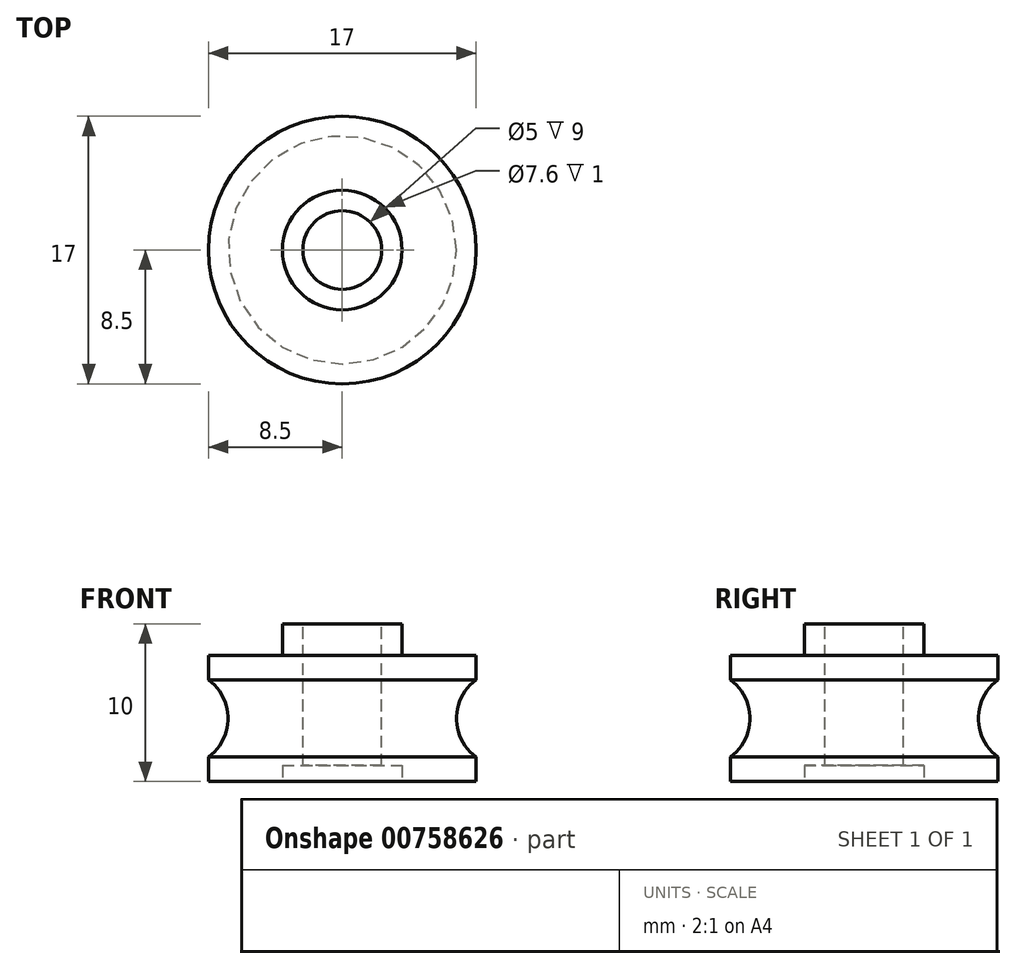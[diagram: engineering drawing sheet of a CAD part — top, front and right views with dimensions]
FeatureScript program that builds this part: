
annotation { "Feature Type Name" : "Feature", "Feature Type Description" : "" }
export const myFeature = defineFeature(function(context is Context, id is Id, definition is map)
    precondition{}
    {
        {
            var Q0;
            Q0=qCreatedBy(makeId("Top.planeOp"),FACE);
            var sketch = newSketch(context, id + "F0", { "sketchPlane" : qUnion([Q0])});
            skCircle(sketch, "E0", {"center": v(0, 0) * mm, "radius": 8.5 * mm});
            skSolve(sketch);
        }
        {
            var Q0;
            Q0=makeQuery(id+"F0.imprint","IMPRINT",FACE,{"disambiguationData":[TD([[makeQuery(id+"F0.imprint","IMPRINT",EDGE,{"derivedFrom":sQuery(id+"F0.wireOp",EDGE,"E0")}),1.0]])]});
            extrude(context, id + "F1", {"entities" : qUnion([Q0]), "depth" : 8 * mm, "offsetDistance" : 25 * mm});
        }
        {
            var Q0;
            Q0=makeQuery(id+"F1.opExtrude","CAP_FACE",FACE,{"disambiguationData":[OSD([sQuery(id+"F0.wireOp",EDGE,"E0")])],"isStart":false});
            var sketch = newSketch(context, id + "F2", { "sketchPlane" : qUnion([Q0])});
            skCircle(sketch, "E1", {"center": v(0, 0) * mm, "radius": 3.8 * mm});
            skSolve(sketch);
        }
        {
            var Q0;
            Q0=makeQuery(id+"F2.imprint","IMPRINT",FACE,{"disambiguationData":[TD([[makeQuery(id+"F2.imprint","IMPRINT",EDGE,{"derivedFrom":sQuery(id+"F2.wireOp",EDGE,"E1")}),1.0]])]});
            extrude(context, id + "F3", {"entities" : qUnion([Q0]), "operationType" : NewBodyOperationType.ADD, "depth" : 2 * mm, "offsetDistance" : 25 * mm});
        }
        {
            var Q0;
            Q0=makeQuery(id+"F3.opExtrude","CAP_FACE",FACE,{"disambiguationData":[OSD([sQuery(id+"F2.wireOp",EDGE,"E1")])],"isStart":false});
            var sketch = newSketch(context, id + "F4", { "sketchPlane" : qUnion([Q0])});
            skCircle(sketch, "E2", {"center": v(0, 0) * mm, "radius": 2.5 * mm});
            skSolve(sketch);
        }
        {
            var Q0;
            Q0=makeQuery(id+"F4.imprint","IMPRINT",FACE,{"disambiguationData":[TD([[makeQuery(id+"F4.imprint","IMPRINT",EDGE,{"derivedFrom":sQuery(id+"F4.wireOp",EDGE,"E2")}),1.0]])]});
            extrude(context, id + "F5", {"entities" : qUnion([Q0]), "operationType" : NewBodyOperationType.REMOVE, "endBound" : BoundingType.THROUGH_ALL, "oppositeDirection" : true, "depth" : 25 * mm, "offsetDistance" : 25 * mm});
        }
        {
            var Q0;
            Q0=qCreatedBy(makeId("Right.planeOp"),FACE);
            var sketch = newSketch(context, id + "F6", { "sketchPlane" : qUnion([Q0])});
            skCircle(sketch, "E3", {"center": v(-10.25, 4) * mm, "radius": 3 * mm});
            skPoint(sketch, "E4.middle", {"position": v(0, 0) * mm});
            skLineSegment(sketch, "E5", {"start": v(0, 0) * mm, "end": v(0, 15.8) * mm});
            skSolve(sketch);
        }
        {
            var Q0;
            Q0=makeQuery(id+"F6.imprint","IMPRINT",FACE,{"disambiguationData":[TD([[makeQuery(id+"F6.imprint","IMPRINT",EDGE,{"derivedFrom":sQuery(id+"F6.wireOp",EDGE,"E3")}),1.0]])]});
            var Q1;
            Q1=sQuery(id+"F6.wireOp",EDGE,"E5");
            revolve(context, id + "F7", {"operationType" : NewBodyOperationType.REMOVE, "surfaceOperationType" : NewSurfaceOperationType.NEW, "entities" : qUnion([Q0]), "axis" : qUnion([Q1]), "revolveType" : RevolveType.FULL, "oppositeDirection" : true});
        }
        {
            var Q0;
            Q0=makeQuery(id+"F1.opExtrude","CAP_FACE",FACE,{"disambiguationData":[OSD([sQuery(id+"F0.wireOp",EDGE,"E0")])],"isStart":true});
            var sketch = newSketch(context, id + "F8", { "sketchPlane" : qUnion([Q0])});
            skCircle(sketch, "E6", {"center": v(0, 0) * mm, "radius": 3.8 * mm});
            skSolve(sketch);
        }
        {
            var Q0;
            Q0=makeQuery(id+"F8.imprint","IMPRINT",FACE,{"disambiguationData":[TD([[makeQuery(id+"F8.imprint","IMPRINT",EDGE,{"derivedFrom":sQuery(id+"F8.wireOp",EDGE,"E6")}),1.0]])]});
            extrude(context, id + "F9", {"entities" : qUnion([Q0]), "operationType" : NewBodyOperationType.REMOVE, "oppositeDirection" : true, "depth" : 1 * mm, "offsetDistance" : 25 * mm});
        }
    });
